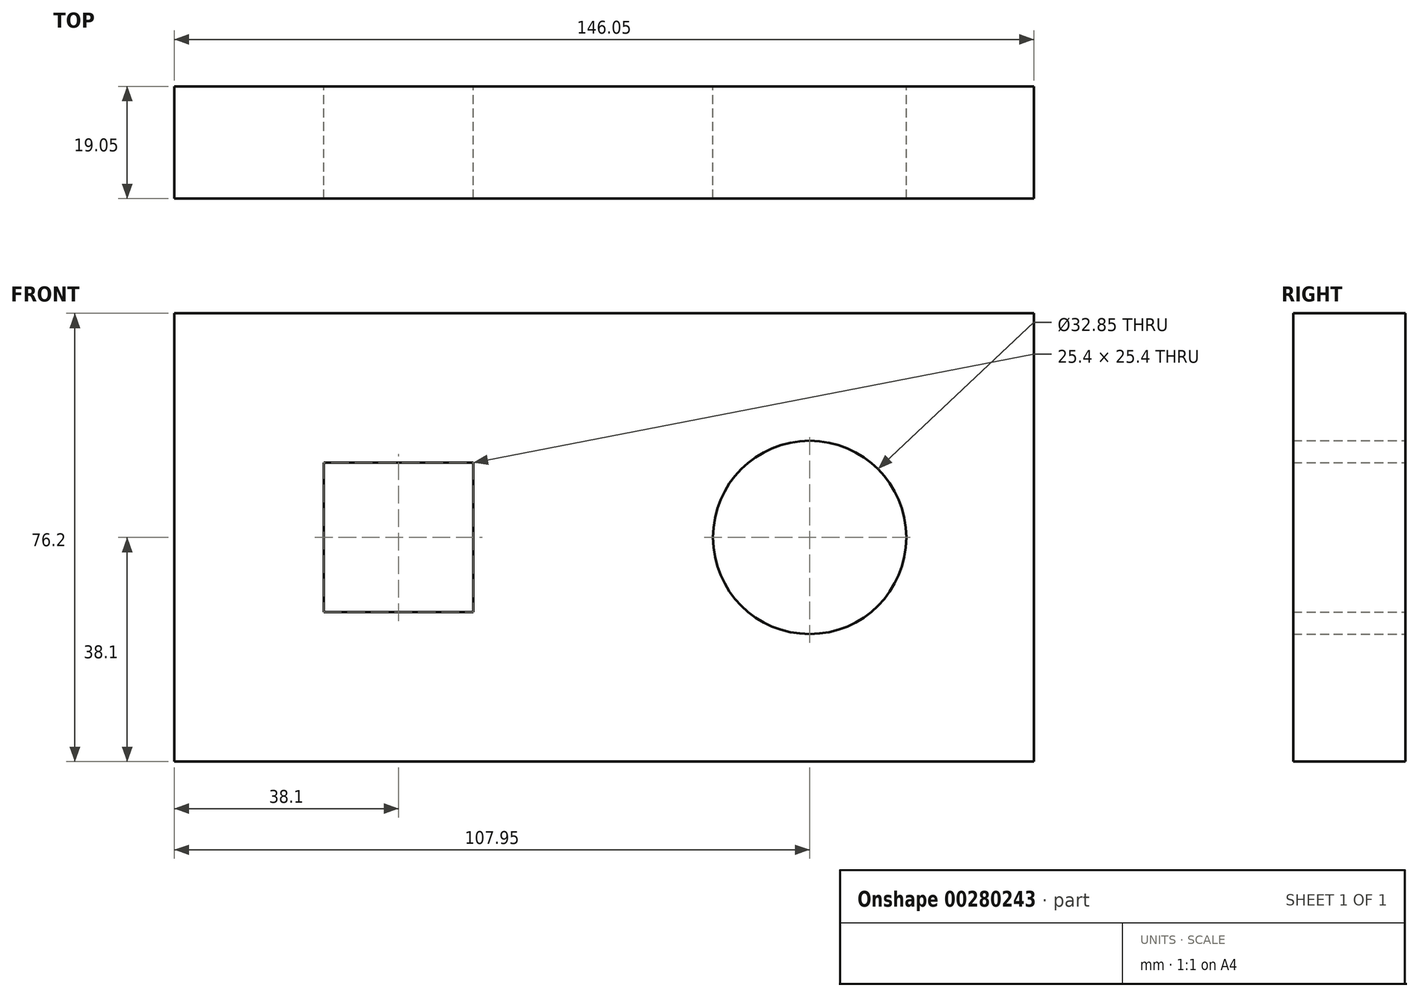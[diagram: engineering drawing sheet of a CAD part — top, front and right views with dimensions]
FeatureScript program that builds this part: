
annotation { "Feature Type Name" : "Feature", "Feature Type Description" : "" }
export const myFeature = defineFeature(function(context is Context, id is Id, definition is map)
    precondition{}
    {
        {
            var Q0;
            Q0=qCreatedBy(makeId("Front.planeOp"),FACE);
            var sketch = newSketch(context, id + "F0", { "sketchPlane" : qUnion([Q0])});
            skLineSegment(sketch, "E0.bottom", {"start": v(0, 0) * mm, "end": v(-146.05, 0) * mm});
            skLineSegment(sketch, "E0.top", {"start": v(0, 76.2) * mm, "end": v(-146.05, 76.2) * mm});
            skLineSegment(sketch, "E0.left", {"start": v(0, 0) * mm, "end": v(0, 76.2) * mm});
            skLineSegment(sketch, "E0.right", {"start": v(-146.05, 0) * mm, "end": v(-146.05, 76.2) * mm});
            skCircle(sketch, "E1", {"center": v(-38.1, 38.1) * mm, "radius": 16.43 * mm});
            skLineSegment(sketch, "E2.bottom", {"start": v(-120.65, 25.4) * mm, "end": v(-95.25, 25.4) * mm});
            skLineSegment(sketch, "E2.top", {"start": v(-120.65, 50.8) * mm, "end": v(-95.25, 50.8) * mm});
            skLineSegment(sketch, "E2.left", {"start": v(-120.65, 25.4) * mm, "end": v(-120.65, 50.8) * mm});
            skLineSegment(sketch, "E2.right", {"start": v(-95.25, 25.4) * mm, "end": v(-95.25, 50.8) * mm});
            skSolve(sketch);
        }
        {
            var Q0;
            Q0 = qSketchRegion(id + "F0", true);
            extrude(context, id + "F1", {"entities" : qUnion([Q0]), "depth" : 19.05 * mm});
        }
    });
